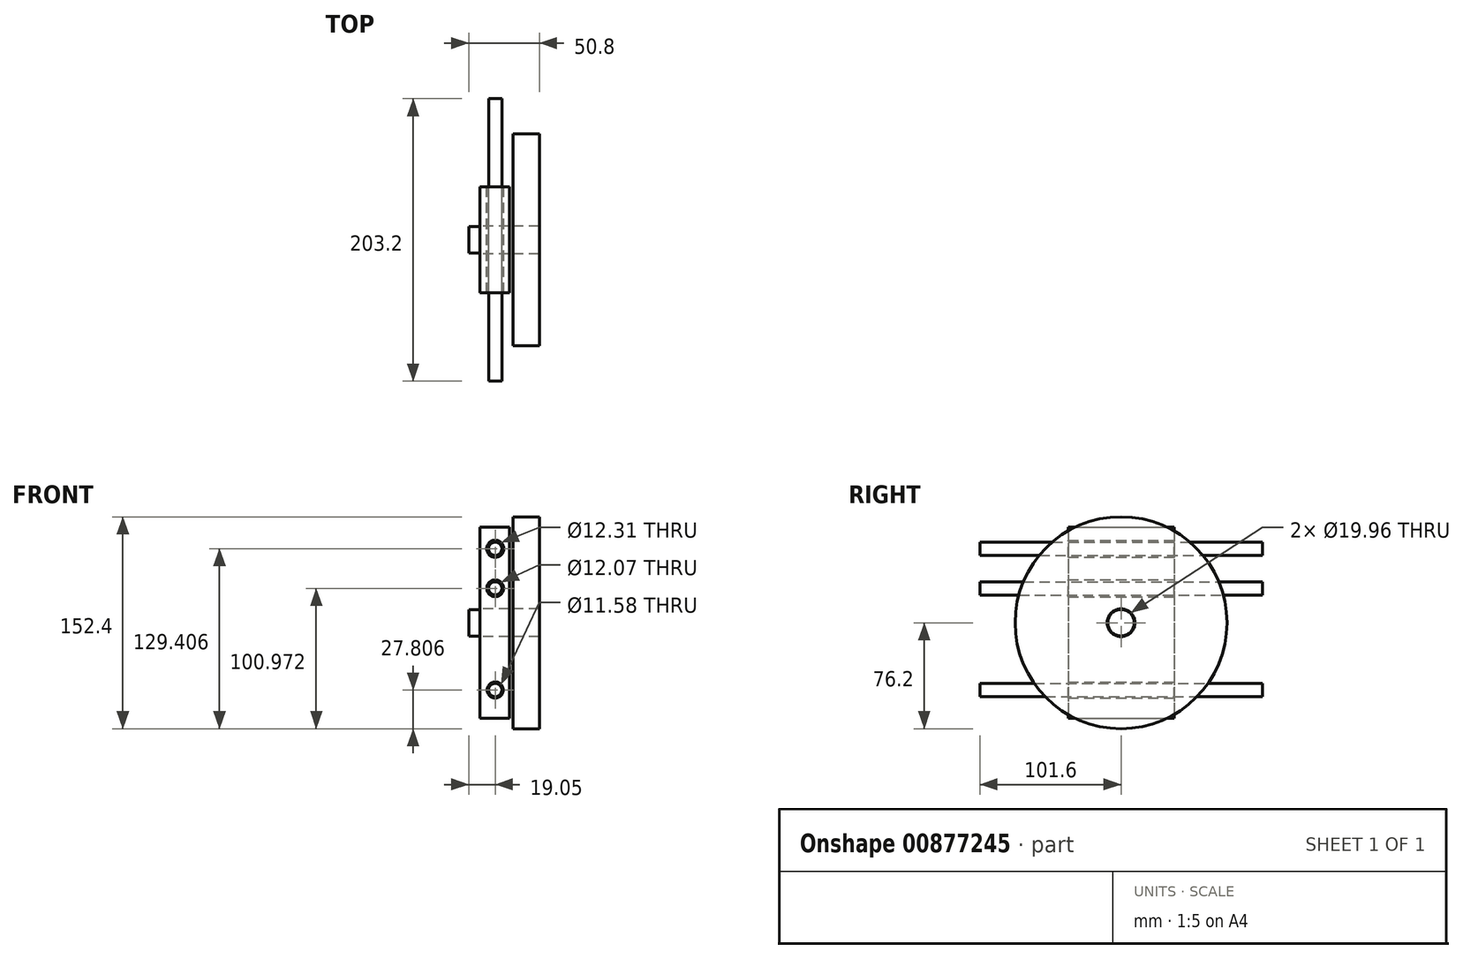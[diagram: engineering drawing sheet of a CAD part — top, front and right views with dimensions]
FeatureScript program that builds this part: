
annotation { "Feature Type Name" : "Feature", "Feature Type Description" : "" }
export const myFeature = defineFeature(function(context is Context, id is Id, definition is map)
    precondition{}
    {
        {
            var Q0;
            Q0=qCreatedBy(makeId("Front.planeOp"),FACE);
            var sketch = newSketch(context, id + "F0", { "sketchPlane" : qUnion([Q0])});
            skCircle(sketch, "E0", {"center": v(-31.75, 53.2) * mm, "radius": 4.76 * mm});
            skCircle(sketch, "E1", {"center": v(-31.75, -48.4) * mm, "radius": 4.76 * mm});
            skLineSegment(sketch, "E2", {"start": v(-31.75, 53.2) * mm, "end": v(-31.75, -48.4) * mm, "construction": true});
            skCircle(sketch, "E3", {"center": v(-31.75, 24.77) * mm, "radius": 4.76 * mm});
            skSolve(sketch);
        }
        {
            var Q0;
            Q0 = qSketchRegion(id + "F0", true);
            extrude(context, id + "F1", {"entities" : qUnion([Q0]), "depth" : 203.2 * mm, "offsetDistance" : 25.4 * mm, "symmetric" : true});
        }
        {
            var Q0;
            Q0=qCreatedBy(makeId("Right.planeOp"),FACE);
            var sketch = newSketch(context, id + "F2", { "sketchPlane" : qUnion([Q0])});
            skCircle(sketch, "E4", {"center": v(0, 0) * mm, "radius": 76.2 * mm});
            skCircle(sketch, "E5", {"center": v(0, 0) * mm, "radius": 9.53 * mm});
            skSolve(sketch);
        }
        {
            var Q0;
            Q0=makeQuery(id+"F2.imprint","IMPRINT",FACE,{"disambiguationData":[TD([[makeQuery(id+"F2.imprint","IMPRINT",EDGE,{"derivedFrom":sQuery(id+"F2.wireOp",EDGE,"E4")}),1.0]])]});
            extrude(context, id + "F3", {"entities" : qUnion([Q0]), "depth" : -19.05 * mm, "offsetDistance" : 25.4 * mm});
        }
        {
            var Q0;
            Q0=makeQuery(id+"F2.imprint","IMPRINT",FACE,{"disambiguationData":[TD([[makeQuery(id+"F2.imprint","IMPRINT",EDGE,{"derivedFrom":sQuery(id+"F2.wireOp",EDGE,"E5")}),1.0]])]});
            extrude(context, id + "F4", {"entities" : qUnion([Q0]), "operationType" : NewBodyOperationType.ADD, "depth" : -50.8 * mm, "offsetDistance" : 25.4 * mm});
        }
        {
            var Q0;
            Q0=qCreatedBy(makeId("Front.planeOp"),FACE);
            var sketch = newSketch(context, id + "F5", { "sketchPlane" : qUnion([Q0])});
            skLineSegment(sketch, "E6.bottom", {"start": v(-42.9, 68.81) * mm, "end": v(-21.59, 68.81) * mm});
            skLineSegment(sketch, "E6.top", {"start": v(-42.9, -68.81) * mm, "end": v(-21.6, -68.81) * mm});
            skLineSegment(sketch, "E6.left", {"start": v(-42.9, 68.81) * mm, "end": v(-42.9, -68.81) * mm});
            skLineSegment(sketch, "E6.right", {"start": v(-21.59, 68.81) * mm, "end": v(-21.59, -68.81) * mm});
            skPoint(sketch, "E6.middle", {"position": v(-32.25, 0) * mm});
            skLineSegment(sketch, "E7.0", {"start": v(-19.05, 76.2) * mm, "end": v(-19.05, -76.2) * mm});
            skLineSegment(sketch, "E8.0", {"start": v(-50.8, 9.53) * mm, "end": v(-50.8, -9.53) * mm});
            skCircle(sketch, "E9.0", {"center": v(-31.75, 53.2) * mm, "radius": 4.76 * mm});
            skCircle(sketch, "E10.0.0", {"center": v(-31.75, 24.77) * mm, "radius": 4.76 * mm});
            skCircle(sketch, "E11.0.0", {"center": v(-31.75, -48.4) * mm, "radius": 4.76 * mm});
            skCircle(sketch, "E12", {"center": v(-31.75, 53.2) * mm, "radius": 6.16 * mm});
            skCircle(sketch, "E13", {"center": v(-31.75, 24.77) * mm, "radius": 6.03 * mm});
            skCircle(sketch, "E14", {"center": v(-31.75, -48.4) * mm, "radius": 5.8 * mm});
            skSolve(sketch);
        }
        {
            var Q0;
            Q0 = qSketchRegion(id + "F5", true);
            extrude(context, id + "F6", {"entities" : qUnion([Q0]), "depth" : 76.2 * mm, "offsetDistance" : 25.4 * mm, "symmetric" : true});
        }
        {
            var Q0;
            Q0=makeQuery(id+"F6.opExtrude","SWEPT_FACE",FACE,{"disambiguationData":[OSD([sQuery(id+"F5.wireOp",EDGE,"E6.left")])]});
            var sketch = newSketch(context, id + "F7", { "sketchPlane" : qUnion([Q0])});
            skCircle(sketch, "E15", {"center": v(0, 0) * mm, "radius": 9.98 * mm});
            skSolve(sketch);
        }
        {
            var Q0;
            Q0 = qSketchRegion(id + "F7", true);
            extrude(context, id + "F8", {"entities" : qUnion([Q0]), "operationType" : NewBodyOperationType.REMOVE, "endBound" : BoundingType.THROUGH_ALL, "oppositeDirection" : true, "depth" : 25.4 * mm, "offsetDistance" : 25.4 * mm});
        }
    });
